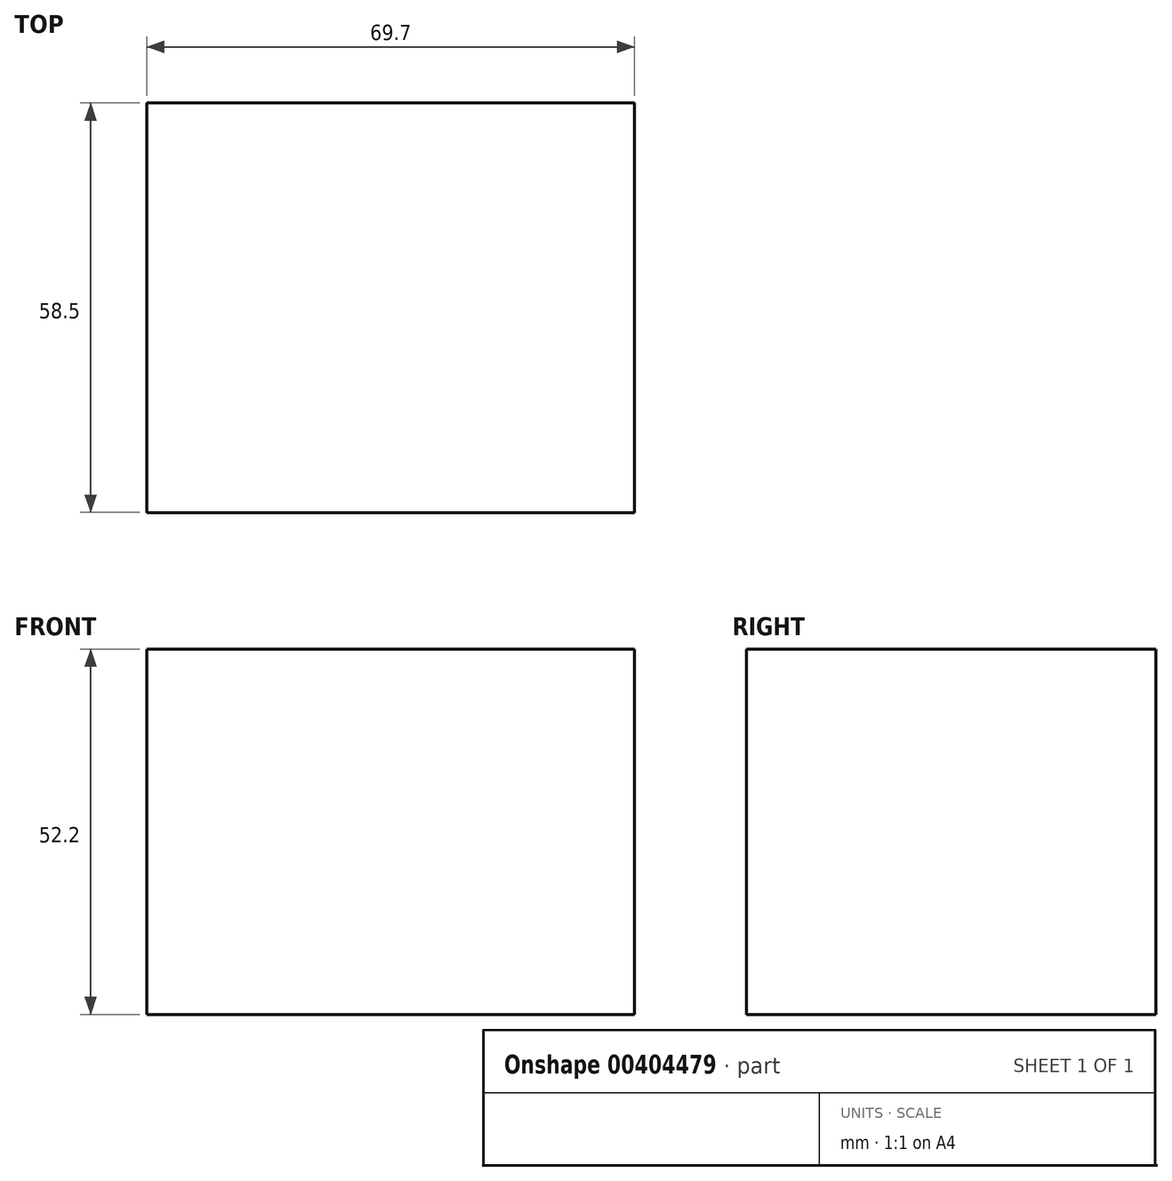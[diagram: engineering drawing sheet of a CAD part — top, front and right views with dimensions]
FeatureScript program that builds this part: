
annotation { "Feature Type Name" : "Feature", "Feature Type Description" : "" }
export const myFeature = defineFeature(function(context is Context, id is Id, definition is map)
    precondition{}
    {
        {
            var Q0;
            Q0=qCreatedBy(makeId("Top.planeOp"),FACE);
            var sketch = newSketch(context, id + "F0", { "sketchPlane" : qUnion([Q0])});
            skLineSegment(sketch, "E0.bottom", {"start": v(-32.36, -28.21) * mm, "end": v(37.34, -28.21) * mm});
            skLineSegment(sketch, "E0.top", {"start": v(-32.36, 30.29) * mm, "end": v(37.34, 30.29) * mm});
            skLineSegment(sketch, "E0.left", {"start": v(-32.36, -28.21) * mm, "end": v(-32.36, 30.29) * mm});
            skLineSegment(sketch, "E0.right", {"start": v(37.34, -28.21) * mm, "end": v(37.34, 30.29) * mm});
            skSolve(sketch);
        }
        {
            var Q0;
            Q0=makeQuery(id+"F0.imprint","IMPRINT",FACE,{"disambiguationData":[TD([[makeQuery(id+"F0.imprint","IMPRINT",EDGE,{"derivedFrom":sQuery(id+"F0.wireOp",EDGE,"E0.bottom")}),1.0]])]});
            var sketch = newSketch(context, id + "F1", { "sketchPlane" : qUnion([Q0])});
            skLineSegment(sketch, "E1.0", {"start": v(37.34, -28.21) * mm, "end": v(37.34, 30.29) * mm});
            skLineSegment(sketch, "E1.1", {"start": v(-32.36, -28.21) * mm, "end": v(37.34, -28.21) * mm});
            skLineSegment(sketch, "E1.2", {"start": v(-32.36, 30.29) * mm, "end": v(37.34, 30.29) * mm});
            skLineSegment(sketch, "E1.3", {"start": v(-32.36, -28.21) * mm, "end": v(-32.36, 30.29) * mm});
            skSolve(sketch);
        }
        {
            var Q0;
            Q0 = qSketchRegion(id + "F1", true);
            extrude(context, id + "F2", {"entities" : qUnion([Q0]), "depth" : 52.2 * mm});
        }
        {
            var Q0;
            Q0 = qSketchRegion(id + "F1", true);
            var sketch = newSketch(context, id + "F3", { "sketchPlane" : qUnion([Q0])});
            skCircle(sketch, "E2", {"center": v(0, 0) * mm, "radius": 18.57 * mm});
            skSolve(sketch);
        }
        {
            var Q0;
            Q0=sQuery(id+"F3.wireOp",EDGE,"E2");
            extrude(context, id + "F4", {"bodyType" : ToolBodyType.SURFACE, "surfaceEntities" : qUnion([Q0]), "depth" : 25.4 * mm});
        }
        {
            var Q0;
            Q0 = qSketchRegion(id + "F1", true);
            var sketch = newSketch(context, id + "F5", { "sketchPlane" : qUnion([Q0])});
            skCircle(sketch, "E3", {"center": v(0, 0) * mm, "radius": 11.58 * mm});
            skSolve(sketch);
        }
        {
            var Q0;
            Q0=sQuery(id+"F5.wireOp",EDGE,"E3");
            extrude(context, id + "F6", {"bodyType" : ToolBodyType.SURFACE, "surfaceEntities" : qUnion([Q0]), "depth" : 90.89 * mm});
        }
    });
